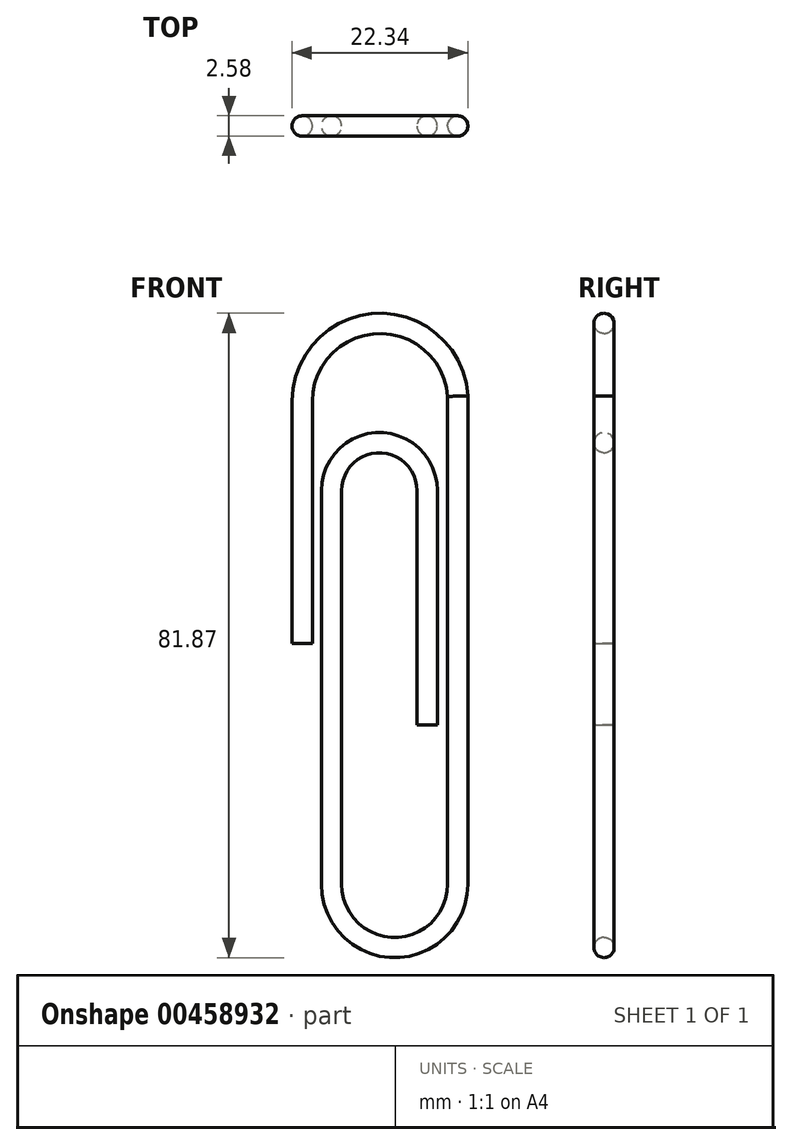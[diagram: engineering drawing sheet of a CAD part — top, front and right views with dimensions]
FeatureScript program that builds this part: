
annotation { "Feature Type Name" : "Feature", "Feature Type Description" : "" }
export const myFeature = defineFeature(function(context is Context, id is Id, definition is map)
    precondition{}
    {
        {
            var Q0;
            Q0=qCreatedBy(makeId("Front.planeOp"),FACE);
            var sketch = newSketch(context, id + "F0", { "sketchPlane" : qUnion([Q0])});
            skLineSegment(sketch, "E0", {"start": v(0, 0) * mm, "end": v(0, 30.77) * mm});
            skArc(sketch, "E1", {"start": v(0, 30.77) * mm, "mid": v(9.57, 40.66) * mm, "end": v(19.76, 31.42) * mm});
            skLineSegment(sketch, "E2", {"start": v(19.76, 31.42) * mm, "end": v(19.76, -30.61) * mm});
            skArc(sketch, "E3", {"start": v(19.76, -30.61) * mm, "mid": v(11.74, -38.63) * mm, "end": v(3.73, -30.61) * mm});
            skLineSegment(sketch, "E4", {"start": v(3.73, -30.61) * mm, "end": v(3.73, 19.44) * mm});
            skArc(sketch, "E5", {"start": v(3.73, 19.44) * mm, "mid": v(9.8, 25.5) * mm, "end": v(15.87, 19.44) * mm});
            skLineSegment(sketch, "E6", {"start": v(15.87, 19.44) * mm, "end": v(15.87, -10.37) * mm});
            skSolve(sketch);
        }
        {
            var Q0;
            Q0=qCreatedBy(makeId("Top.planeOp"),FACE);
            var sketch = newSketch(context, id + "F1", { "sketchPlane" : qUnion([Q0])});
            skCircle(sketch, "E7", {"center": v(0, 0) * mm, "radius": 1.29 * mm});
            skSolve(sketch);
        }
        {
            var Q0;
            Q0=makeQuery(id+"F1.imprint","IMPRINT",FACE,{"disambiguationData":[TD([[makeQuery(id+"F1.imprint","IMPRINT",EDGE,{"derivedFrom":sQuery(id+"F1.wireOp",EDGE,"E7")}),1.0]])]});
            var Q1;
            Q1=sQuery(id+"F0.wireOp",EDGE,"E0");
            var Q2;
            Q2=sQuery(id+"F0.wireOp",EDGE,"E1");
            var Q3;
            Q3=sQuery(id+"F0.wireOp",EDGE,"E2");
            var Q4;
            Q4=sQuery(id+"F0.wireOp",EDGE,"E3");
            var Q5;
            Q5=sQuery(id+"F0.wireOp",EDGE,"E4");
            var Q6;
            Q6=sQuery(id+"F0.wireOp",EDGE,"E5");
            var Q7;
            Q7=sQuery(id+"F0.wireOp",EDGE,"E6");
            sweep(context, id + "F2", {"profiles" : qUnion([Q0]), "path" : qUnion([Q1, Q2, Q3, Q4, Q5, Q6, Q7])});
        }
    });
